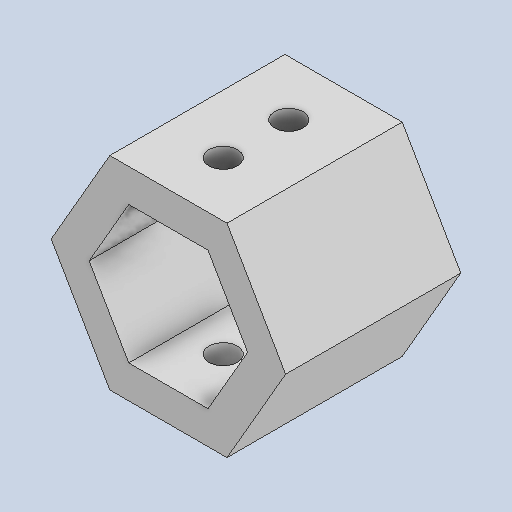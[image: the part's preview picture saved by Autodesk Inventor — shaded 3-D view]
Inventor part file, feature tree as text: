
AUTODESK INVENTOR PART (.ipt)
format: ipt  version: 2022 (Build 260153000, 153)  size: 132,608 bytes
history: native  units: mm
features: extrude x2, sketch x2, projected_geometry x1
ambient origin geometry x8: Origin, YZ Plane, XZ Plane, XY Plane, X Axis, Y Axis, Z Axis, Center Point
bodies: Body1 (feature_tree)
feature tree (5):
  extrude  "Extrusion3"  Depth=60.0mm TaperAngle=360.0deg
  extrude  "Extrusion4"  Depth=1.5mm
  sketch  "Sketch4"  dims[d8=6.2mm d9=60.0mm d11=360.0deg]
  sketch  "Sketch5"  dims[d13=0.45mm d14=1.5mm d15=8.0mm d16=0.0mm d17=1.3mm d18=2.5mm d19=2.5mm d20=10.0mm d21=0.0mm d22=0.5mm d23=0.872665mm]
  projected_geometry  "Projected Loop2"
